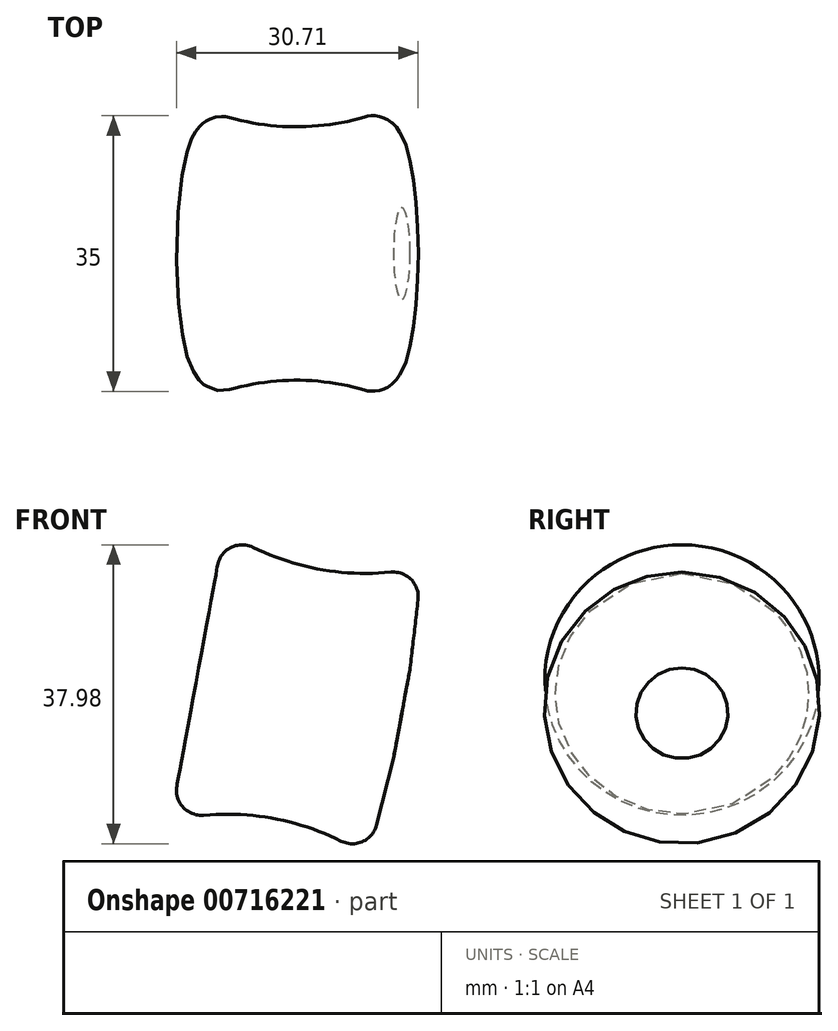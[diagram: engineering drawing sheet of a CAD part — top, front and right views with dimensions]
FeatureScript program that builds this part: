
annotation { "Feature Type Name" : "Feature", "Feature Type Description" : "" }
export const myFeature = defineFeature(function(context is Context, id is Id, definition is map)
    precondition{}
    {
        {
            var Q0;
            Q0=qCreatedBy(makeId("Front.planeOp"),FACE);
            var sketch = newSketch(context, id + "F0", { "sketchPlane" : qUnion([Q0])});
            skArc(sketch, "E0", {"start": v(-60.6, -6.4) * mm, "mid": v(-52.07, -9.2) * mm, "end": v(-43.1, -9.55) * mm});
            skLineSegment(sketch, "E1", {"start": v(-65.11, -8.68) * mm, "end": v(-66.63, -16.93) * mm});
            skLineSegment(sketch, "E2", {"start": v(-66.63, -16.93) * mm, "end": v(-40.65, -21.72) * mm});
            skLineSegment(sketch, "E3", {"start": v(-40.65, -21.72) * mm, "end": v(-39.64, -13.08) * mm});
            skPoint(sketch, "E4.visualSharp", {"position": v(-39.15, -8.9) * mm});
            skArc(sketch, "E4.filletArc", {"start": v(-39.64, -13.08) * mm, "mid": v(-40.53, -10.49) * mm, "end": v(-43.1, -9.55) * mm});
            skPoint(sketch, "E5.visualSharp", {"position": v(-64.3, -4.27) * mm});
            skArc(sketch, "E5.filletArc", {"start": v(-60.6, -6.4) * mm, "mid": v(-63.42, -6.42) * mm, "end": v(-65.11, -8.68) * mm});
            skLineSegment(sketch, "E6", {"start": v(-66.63, -16.93) * mm, "end": v(-67.7, -22.69) * mm});
            skLineSegment(sketch, "E7", {"start": v(-67.7, -22.69) * mm, "end": v(-41.7, -27.48) * mm});
            skLineSegment(sketch, "E8", {"start": v(-41.7, -27.48) * mm, "end": v(-40.65, -21.72) * mm});
            skSolve(sketch);
        }
        {
            var Q0;
            Q0 = qSketchRegion(id + "F0", true);
            var Q1;
            Q1=sQuery(id+"F0.wireOp",EDGE,"E7");
            revolve(context, id + "F1", {"surfaceOperationType" : NewSurfaceOperationType.NEW, "entities" : qUnion([Q0]), "axis" : qUnion([Q1]), "revolveType" : RevolveType.FULL});
        }
    });
